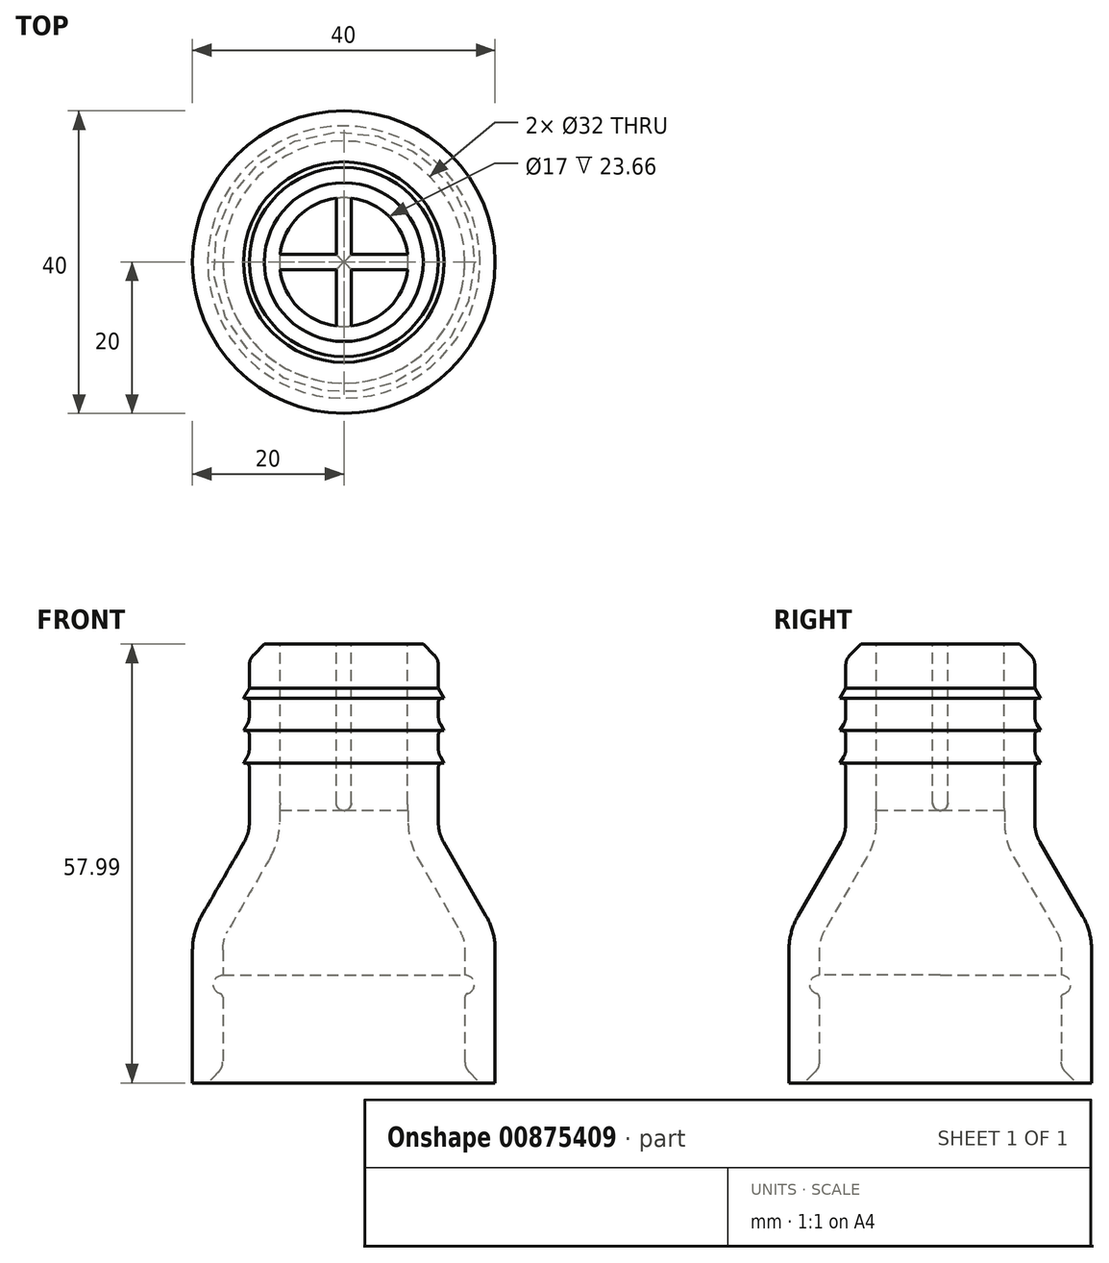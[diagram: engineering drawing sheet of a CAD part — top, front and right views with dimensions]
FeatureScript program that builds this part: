
annotation { "Feature Type Name" : "Feature", "Feature Type Description" : "" }
export const myFeature = defineFeature(function(context is Context, id is Id, definition is map)
    precondition{}
    {
        {
            var Q0;
            Q0=qCreatedBy(makeId("Front.planeOp"),FACE);
            var sketch = newSketch(context, id + "F0", { "sketchPlane" : qUnion([Q0])});
            skLineSegment(sketch, "E0", {"start": v(0, 0) * mm, "end": v(0, 58) * mm});
            skLineSegment(sketch, "E1", {"start": v(20, 0) * mm, "end": v(20, 20) * mm});
            skLineSegment(sketch, "E2", {"start": v(20, 20) * mm, "end": v(12.5, 33) * mm});
            skLineSegment(sketch, "E3", {"start": v(12.5, 33) * mm, "end": v(12.5, 58) * mm});
            skLineSegment(sketch, "E4", {"start": v(0, 0) * mm, "end": v(20, 0) * mm});
            skLineSegment(sketch, "E5", {"start": v(12.5, 58) * mm, "end": v(0, 58) * mm});
            skSolve(sketch);
        }
        {
            var Q0;
            Q0 = qSketchRegion(id + "F0", true);
            var Q1;
            Q1=sQuery(id+"F0.wireOp",EDGE,"E0");
            revolve(context, id + "F1", {"surfaceOperationType" : NewSurfaceOperationType.NEW, "entities" : qUnion([Q0]), "axis" : qUnion([Q1]), "revolveType" : RevolveType.FULL});
        }
        {
            var Q0;
            Q0=makeQuery(id+"F1.opRevolve","SWEPT_EDGE",EDGE,{"disambiguationData":[OSD([sQuery(id+"F0.wireOp",EDGE,"E2"),sQuery(id+"F0.wireOp",EDGE,"E3")])]});
            fillet(context, id + "F2", {"entities" : qUnion([Q0]), "radius" : 5 * mm, "tangentPropagation" : true, "allowEdgeOverflow" : false});
        }
        {
            var Q0;
            Q0=makeQuery(id+"F1.opRevolve","SWEPT_EDGE",EDGE,{"disambiguationData":[OSD([sQuery(id+"F0.wireOp",EDGE,"E1"),sQuery(id+"F0.wireOp",EDGE,"E2")])]});
            fillet(context, id + "F3", {"entities" : qUnion([Q0]), "radius" : 9 * mm, "tangentPropagation" : true, "allowEdgeOverflow" : false});
        }
        {
            var Q0;
            Q0=makeQuery(id+"F1.opRevolve","SWEPT_FACE",FACE,{"disambiguationData":[OSD([sQuery(id+"F0.wireOp",EDGE,"E4")])]});
            var Q1;
            Q1=makeQuery(id+"F1.opRevolve","SWEPT_FACE",FACE,{"disambiguationData":[OSD([sQuery(id+"F0.wireOp",EDGE,"E5")])]});
            shell(context, id + "F4", {"entities" : qUnion([Q0, Q1]), "thickness" : 4 * mm});
        }
        {
            var Q0;
            Q0=qCreatedBy(makeId("Front.planeOp"),FACE);
            var sketch = newSketch(context, id + "F5", { "sketchPlane" : qUnion([Q0])});
            skCircle(sketch, "E6", {"center": v(16, 13) * mm, "radius": 1.25 * mm});
            skLineSegment(sketch, "E7", {"start": v(16, 0) * mm, "end": v(16, 17.59) * mm});
            skLineSegment(sketch, "E8", {"start": v(-16, 17.59) * mm, "end": v(-16, 0) * mm});
            skLineSegment(sketch, "E9", {"start": v(0, 0) * mm, "end": v(0, 10.29) * mm});
            skSolve(sketch);
        }
        {
            var Q0;
            {var subQ0=sQuery(id+"F5.wireOp",EDGE,"E7");var subQ1=sQuery(id+"F5.wireOp",EDGE,"E6");var subQ2=makeQuery(id+"F5.imprint","INTERSECT",VERTEX,{"disambiguationData":[OD(0.0)],"derivedFrom":[subQ1,subQ0]});Q0=makeQuery(id+"F5.imprint","IMPRINT",FACE,{"disambiguationData":[TD([[makeQuery(id+"F5.imprint","IMPRINT",EDGE,{"disambiguationData":[TD([[subQ2,1.0]])],"derivedFrom":subQ1}),1.0]])]});}
            var Q1;
            {var subQ0=sQuery(id+"F5.wireOp",EDGE,"E7");var subQ1=sQuery(id+"F5.wireOp",EDGE,"E6");var subQ2=makeQuery(id+"F5.imprint","INTERSECT",VERTEX,{"disambiguationData":[OD(0.0)],"derivedFrom":[subQ1,subQ0]});Q1=makeQuery(id+"F5.imprint","IMPRINT",FACE,{"disambiguationData":[TD([[makeQuery(id+"F5.imprint","IMPRINT",EDGE,{"disambiguationData":[TD([[subQ2,-1.0]])],"derivedFrom":subQ1}),1.0]])]});}
            var Q2;
            Q2=sQuery(id+"F5.wireOp",EDGE,"E9");
            revolve(context, id + "F6", {"operationType" : NewBodyOperationType.REMOVE, "surfaceOperationType" : NewSurfaceOperationType.NEW, "entities" : qUnion([Q0, Q1]), "axis" : qUnion([Q2]), "revolveType" : RevolveType.FULL, "oppositeDirection" : true});
        }
        {
            var Q0;
            Q0=makeQuery(id+"F4.opShell","OFFSET_EDGE",EDGE,{"disambiguationData":[OSD([sQuery(id+"F0.wireOp",EDGE,"E1"),sQuery(id+"F0.wireOp",EDGE,"E4")])]});
            var Q1;
            Q1=makeQuery(id+"F1.opRevolve","SWEPT_EDGE",EDGE,{"disambiguationData":[OSD([sQuery(id+"F0.wireOp",EDGE,"E3"),sQuery(id+"F0.wireOp",EDGE,"E5")])]});
            chamfer(context, id + "F7", {"entities" : qUnion([Q0, Q1]), "width" : 2 * mm, "tangentPropagation" : true});
        }
        {
            var Q0;
            {var subQ0=sQuery(id+"F0.wireOp",EDGE,"E4");var subQ1=sQuery(id+"F0.wireOp",EDGE,"E1");Q0=makeQuery(id+"F7.opChamfer","BLEND_EDGE",EDGE,{"blendedFrom":[makeQuery(id+"F4.opShell","OFFSET_EDGE",EDGE,{"disambiguationData":[OSD([subQ1,subQ0])]}),makeQuery(id+"F6.boolean.opBoolean","SPLIT",FACE,{"disambiguationData":[TD([makeQuery(id+"F1.opRevolve","SWEPT_FACE",FACE,{"disambiguationData":[OSD([subQ0])]})])],"derivedFrom":makeQuery(id+"F4.opShell","OFFSET_FACE",FACE,{"disambiguationData":[OSD([subQ1])]})})],"blendedInto":[makeQuery(id+"F6.boolean.opBoolean","SPLIT",FACE,{"disambiguationData":[TD([makeQuery(id+"F1.opRevolve","SWEPT_FACE",FACE,{"disambiguationData":[OSD([subQ0])]})])],"derivedFrom":makeQuery(id+"F4.opShell","OFFSET_FACE",FACE,{"disambiguationData":[OSD([subQ1])]})})]});}
            var Q1;
            {var subQ0=sQuery(id+"F0.wireOp",EDGE,"E3");Q1=makeQuery(id+"F7.opChamfer","BLEND_EDGE",EDGE,{"blendedFrom":[makeQuery(id+"F1.opRevolve","SWEPT_EDGE",EDGE,{"disambiguationData":[OSD([subQ0,sQuery(id+"F0.wireOp",EDGE,"E5")])]}),makeQuery(id+"F1.opRevolve","SWEPT_FACE",FACE,{"disambiguationData":[OSD([subQ0])]})],"blendedInto":[makeQuery(id+"F1.opRevolve","SWEPT_FACE",FACE,{"disambiguationData":[OSD([subQ0])]})]});}
            fillet(context, id + "F8", {"entities" : qUnion([Q0, Q1]), "radius" : 2 * mm, "tangentPropagation" : true, "allowEdgeOverflow" : false});
        }
        {
            var Q0;
            Q0=qCreatedBy(makeId("Front.planeOp"),FACE);
            var sketch = newSketch(context, id + "F9", { "sketchPlane" : qUnion([Q0])});
            skLineSegment(sketch, "E10", {"start": v(12.5, 34.33) * mm, "end": v(12.5, 55.16) * mm});
            skLineSegment(sketch, "E11", {"start": v(-12.5, 55.16) * mm, "end": v(-12.5, 34.33) * mm});
            skLineSegment(sketch, "E12", {"start": v(12.5, 52.16) * mm, "end": v(13.25, 50.86) * mm});
            skLineSegment(sketch, "E13", {"start": v(13.25, 50.86) * mm, "end": v(12.5, 50.86) * mm});
            skLineSegment(sketch, "E14", {"start": v(12.5, 47.86) * mm, "end": v(13.25, 46.56) * mm});
            skLineSegment(sketch, "E15", {"start": v(13.25, 46.56) * mm, "end": v(12.5, 46.56) * mm});
            skLineSegment(sketch, "E16", {"start": v(12.5, 43.56) * mm, "end": v(13.25, 42.26) * mm});
            skLineSegment(sketch, "E17", {"start": v(13.25, 42.26) * mm, "end": v(12.5, 42.26) * mm});
            skLineSegment(sketch, "E18", {"start": v(0, 0) * mm, "end": v(0, 69.05) * mm});
            skSolve(sketch);
        }
        {
            var Q0;
            Q0 = qSketchRegion(id + "F9", true);
            var Q1;
            Q1=sQuery(id+"F9.wireOp",EDGE,"E18");
            revolve(context, id + "F10", {"operationType" : NewBodyOperationType.ADD, "surfaceOperationType" : NewSurfaceOperationType.NEW, "entities" : qUnion([Q0]), "axis" : qUnion([Q1]), "revolveType" : RevolveType.FULL});
        }
        {
            var Q0;
            Q0=makeQuery(id+"F10.opRevolve","SWEPT_EDGE",EDGE,{"disambiguationData":[OSD([sQuery(id+"F9.wireOp",EDGE,"E10"),sQuery(id+"F9.wireOp",EDGE,"E12")])]});
            var Q1;
            Q1=makeQuery(id+"F10.opRevolve","SWEPT_EDGE",EDGE,{"disambiguationData":[OSD([sQuery(id+"F9.wireOp",EDGE,"E10"),sQuery(id+"F9.wireOp",EDGE,"E14")])]});
            var Q2;
            Q2=makeQuery(id+"F10.opRevolve","SWEPT_EDGE",EDGE,{"disambiguationData":[OSD([sQuery(id+"F9.wireOp",EDGE,"E10"),sQuery(id+"F9.wireOp",EDGE,"E16")])]});
            fillet(context, id + "F11", {"entities" : qUnion([Q0, Q1, Q2]), "radius" : 2 * mm, "tangentPropagation" : true, "allowEdgeOverflow" : false});
        }
        {
            var Q0;
            Q0=makeQuery(id+"F10.opRevolve","SWEPT_EDGE",EDGE,{"disambiguationData":[OSD([sQuery(id+"F9.wireOp",EDGE,"E10"),sQuery(id+"F9.wireOp",EDGE,"E13")])]});
            var Q1;
            Q1=makeQuery(id+"F10.opRevolve","SWEPT_EDGE",EDGE,{"disambiguationData":[OSD([sQuery(id+"F9.wireOp",EDGE,"E10"),sQuery(id+"F9.wireOp",EDGE,"E15")])]});
            var Q2;
            Q2=makeQuery(id+"F10.opRevolve","SWEPT_EDGE",EDGE,{"disambiguationData":[OSD([sQuery(id+"F9.wireOp",EDGE,"E10"),sQuery(id+"F9.wireOp",EDGE,"E17")])]});
            fillet(context, id + "F12", {"entities" : qUnion([Q0, Q1, Q2]), "radius" : 0.5 * mm, "tangentPropagation" : true, "allowEdgeOverflow" : false});
        }
        {
            var Q0;
            Q0=makeQuery(id+"F6.boolean.opBoolean","INTERSECT",EDGE,{"disambiguationData":[OD(0.0)],"derivedFrom":[makeQuery(id+"F4.opShell","OFFSET_FACE",FACE,{"disambiguationData":[OSD([sQuery(id+"F0.wireOp",EDGE,"E1")])]}),makeQuery(id+"F6.opRevolve","SWEPT_FACE",FACE,{"disambiguationData":[OSD([sQuery(id+"F5.wireOp",EDGE,"E6")])]})]});
            fillet(context, id + "F13", {"entities" : qUnion([Q0]), "radius" : 0.5 * mm, "tangentPropagation" : true, "allowEdgeOverflow" : false});
        }
        {
            var Q0;
            Q0=makeQuery(id+"F1.opRevolve","SWEPT_FACE",FACE,{"disambiguationData":[OSD([sQuery(id+"F0.wireOp",EDGE,"E5")])]});
            var sketch = newSketch(context, id + "F14", { "sketchPlane" : qUnion([Q0])});
            skLineSegment(sketch, "E19", {"start": v(-9.32, 0) * mm, "end": v(9.5, 0) * mm, "construction": true});
            skLineSegment(sketch, "E20", {"start": v(0, 9.57) * mm, "end": v(0, -9.64) * mm, "construction": true});
            skLineSegment(sketch, "E21.0", {"start": v(-9.32, -1) * mm, "end": v(9.5, -1) * mm});
            skLineSegment(sketch, "E22.0", {"start": v(-9.32, 1) * mm, "end": v(9.5, 1) * mm});
            skLineSegment(sketch, "E23.0", {"start": v(-1, 9.57) * mm, "end": v(-1, -9.64) * mm});
            skLineSegment(sketch, "E24.0", {"start": v(1, 9.57) * mm, "end": v(1, -9.64) * mm});
            skLineSegment(sketch, "E25", {"start": v(-9.32, -1) * mm, "end": v(-9.32, 1) * mm});
            skLineSegment(sketch, "E26", {"start": v(1, 9.57) * mm, "end": v(-1, 9.57) * mm});
            skLineSegment(sketch, "E27", {"start": v(9.5, 1) * mm, "end": v(9.5, -1) * mm});
            skLineSegment(sketch, "E28", {"start": v(1, -9.64) * mm, "end": v(-1, -9.64) * mm});
            skSolve(sketch);
        }
        {
            var Q0;
            {var subQ0=sQuery(id+"F14.wireOp",EDGE,"E23.0");var subQ1=sQuery(id+"F14.wireOp",EDGE,"E21.0");var subQ2=makeQuery(id+"F14.imprint","INTERSECT",VERTEX,{"derivedFrom":[subQ1,subQ0]});Q0=makeQuery(id+"F14.imprint","IMPRINT",FACE,{"disambiguationData":[TD([[makeQuery(id+"F14.imprint","IMPRINT",EDGE,{"disambiguationData":[TD([[subQ2,1.0]])],"derivedFrom":subQ0}),-1.0]])]});}
            var Q1;
            {var subQ0=sQuery(id+"F14.wireOp",EDGE,"E23.0");var subQ1=sQuery(id+"F14.wireOp",EDGE,"E21.0");var subQ2=makeQuery(id+"F14.imprint","INTERSECT",VERTEX,{"derivedFrom":[subQ1,subQ0]});Q1=makeQuery(id+"F14.imprint","IMPRINT",FACE,{"disambiguationData":[TD([[makeQuery(id+"F14.imprint","IMPRINT",EDGE,{"disambiguationData":[TD([[subQ2,-1.0]])],"derivedFrom":subQ1}),1.0]])]});}
            var Q2;
            {var subQ0=sQuery(id+"F14.wireOp",EDGE,"E23.0");var subQ1=sQuery(id+"F14.wireOp",EDGE,"E22.0");var subQ2=makeQuery(id+"F14.imprint","INTERSECT",VERTEX,{"derivedFrom":[subQ1,subQ0]});Q2=makeQuery(id+"F14.imprint","IMPRINT",FACE,{"disambiguationData":[TD([[makeQuery(id+"F14.imprint","IMPRINT",EDGE,{"disambiguationData":[TD([[subQ2,-1.0]])],"derivedFrom":subQ1}),1.0]])]});}
            var Q3;
            {var subQ0=sQuery(id+"F14.wireOp",EDGE,"E24.0");var subQ1=sQuery(id+"F14.wireOp",EDGE,"E21.0");var subQ2=makeQuery(id+"F14.imprint","INTERSECT",VERTEX,{"derivedFrom":[subQ1,subQ0]});Q3=makeQuery(id+"F14.imprint","IMPRINT",FACE,{"disambiguationData":[TD([[makeQuery(id+"F14.imprint","IMPRINT",EDGE,{"disambiguationData":[TD([[subQ2,1.0]])],"derivedFrom":subQ0}),1.0]])]});}
            var Q4;
            {var subQ0=sQuery(id+"F14.wireOp",EDGE,"E23.0");var subQ1=sQuery(id+"F14.wireOp",EDGE,"E21.0");var subQ2=makeQuery(id+"F14.imprint","INTERSECT",VERTEX,{"derivedFrom":[subQ1,subQ0]});Q4=makeQuery(id+"F14.imprint","IMPRINT",FACE,{"disambiguationData":[TD([[makeQuery(id+"F14.imprint","IMPRINT",EDGE,{"disambiguationData":[TD([[subQ2,-1.0]])],"derivedFrom":subQ1}),-1.0]])]});}
            extrude(context, id + "F15", {"entities" : qUnion([Q0, Q1, Q2, Q3, Q4]), "operationType" : NewBodyOperationType.ADD, "oppositeDirection" : true, "depth" : 22 * mm, "offsetDistance" : 25 * mm});
        }
        {
            var Q0;
            {var subQ0=sQuery(id+"F14.wireOp",EDGE,"E24.0");Q0=makeQuery(id+"F15.opExtrude","CAP_EDGE",EDGE,{"disambiguationData":[OSD([subQ0]),TDD([makeQuery(id+"F14.imprint","IMPRINT",EDGE,{"disambiguationData":[TD([[makeQuery(id+"F14.imprint","INTERSECT",VERTEX,{"derivedFrom":[sQuery(id+"F14.wireOp",EDGE,"E22.0"),subQ0]}),1.0]])],"derivedFrom":subQ0})])],"isStart":false});}
            var Q1;
            {var subQ0=sQuery(id+"F14.wireOp",EDGE,"E23.0");Q1=makeQuery(id+"F15.opExtrude","CAP_EDGE",EDGE,{"disambiguationData":[OSD([subQ0]),TDD([makeQuery(id+"F14.imprint","IMPRINT",EDGE,{"disambiguationData":[TD([[makeQuery(id+"F14.imprint","INTERSECT",VERTEX,{"derivedFrom":[sQuery(id+"F14.wireOp",EDGE,"E22.0"),subQ0]}),1.0]])],"derivedFrom":subQ0})])],"isStart":false});}
            var Q2;
            {var subQ0=sQuery(id+"F14.wireOp",EDGE,"E22.0");Q2=makeQuery(id+"F15.opExtrude","CAP_EDGE",EDGE,{"disambiguationData":[OSD([subQ0]),TDD([makeQuery(id+"F14.imprint","IMPRINT",EDGE,{"disambiguationData":[TD([[makeQuery(id+"F14.imprint","INTERSECT",VERTEX,{"derivedFrom":[subQ0,sQuery(id+"F14.wireOp",EDGE,"E24.0")]}),-1.0]])],"derivedFrom":subQ0})])],"isStart":false});}
            var Q3;
            {var subQ0=sQuery(id+"F14.wireOp",EDGE,"E21.0");Q3=makeQuery(id+"F15.opExtrude","CAP_EDGE",EDGE,{"disambiguationData":[OSD([subQ0]),TDD([makeQuery(id+"F14.imprint","IMPRINT",EDGE,{"disambiguationData":[TD([[makeQuery(id+"F14.imprint","INTERSECT",VERTEX,{"derivedFrom":[subQ0,sQuery(id+"F14.wireOp",EDGE,"E24.0")]}),-1.0]])],"derivedFrom":subQ0})])],"isStart":false});}
            var Q4;
            {var subQ0=sQuery(id+"F14.wireOp",EDGE,"E24.0");Q4=makeQuery(id+"F15.opExtrude","CAP_EDGE",EDGE,{"disambiguationData":[OSD([subQ0]),TDD([makeQuery(id+"F14.imprint","IMPRINT",EDGE,{"disambiguationData":[TD([[makeQuery(id+"F14.imprint","INTERSECT",VERTEX,{"derivedFrom":[sQuery(id+"F14.wireOp",EDGE,"E21.0"),subQ0]}),-1.0]])],"derivedFrom":subQ0})])],"isStart":false});}
            var Q5;
            {var subQ0=sQuery(id+"F14.wireOp",EDGE,"E23.0");Q5=makeQuery(id+"F15.opExtrude","CAP_EDGE",EDGE,{"disambiguationData":[OSD([subQ0]),TDD([makeQuery(id+"F14.imprint","IMPRINT",EDGE,{"disambiguationData":[TD([[makeQuery(id+"F14.imprint","INTERSECT",VERTEX,{"derivedFrom":[sQuery(id+"F14.wireOp",EDGE,"E21.0"),subQ0]}),-1.0]])],"derivedFrom":subQ0})])],"isStart":false});}
            var Q6;
            {var subQ0=sQuery(id+"F14.wireOp",EDGE,"E21.0");Q6=makeQuery(id+"F15.opExtrude","CAP_EDGE",EDGE,{"disambiguationData":[OSD([subQ0]),TDD([makeQuery(id+"F14.imprint","IMPRINT",EDGE,{"disambiguationData":[TD([[makeQuery(id+"F14.imprint","INTERSECT",VERTEX,{"derivedFrom":[subQ0,sQuery(id+"F14.wireOp",EDGE,"E23.0")]}),1.0]])],"derivedFrom":subQ0})])],"isStart":false});}
            var Q7;
            {var subQ0=sQuery(id+"F14.wireOp",EDGE,"E22.0");Q7=makeQuery(id+"F15.opExtrude","CAP_EDGE",EDGE,{"disambiguationData":[OSD([subQ0]),TDD([makeQuery(id+"F14.imprint","IMPRINT",EDGE,{"disambiguationData":[TD([[makeQuery(id+"F14.imprint","INTERSECT",VERTEX,{"derivedFrom":[subQ0,sQuery(id+"F14.wireOp",EDGE,"E23.0")]}),1.0]])],"derivedFrom":subQ0})])],"isStart":false});}
            fillet(context, id + "F16", {"entities" : qUnion([Q0, Q1, Q2, Q3, Q4, Q5, Q6, Q7]), "radius" : 1 * mm, "tangentPropagation" : true, "allowEdgeOverflow" : false});
        }
    });
